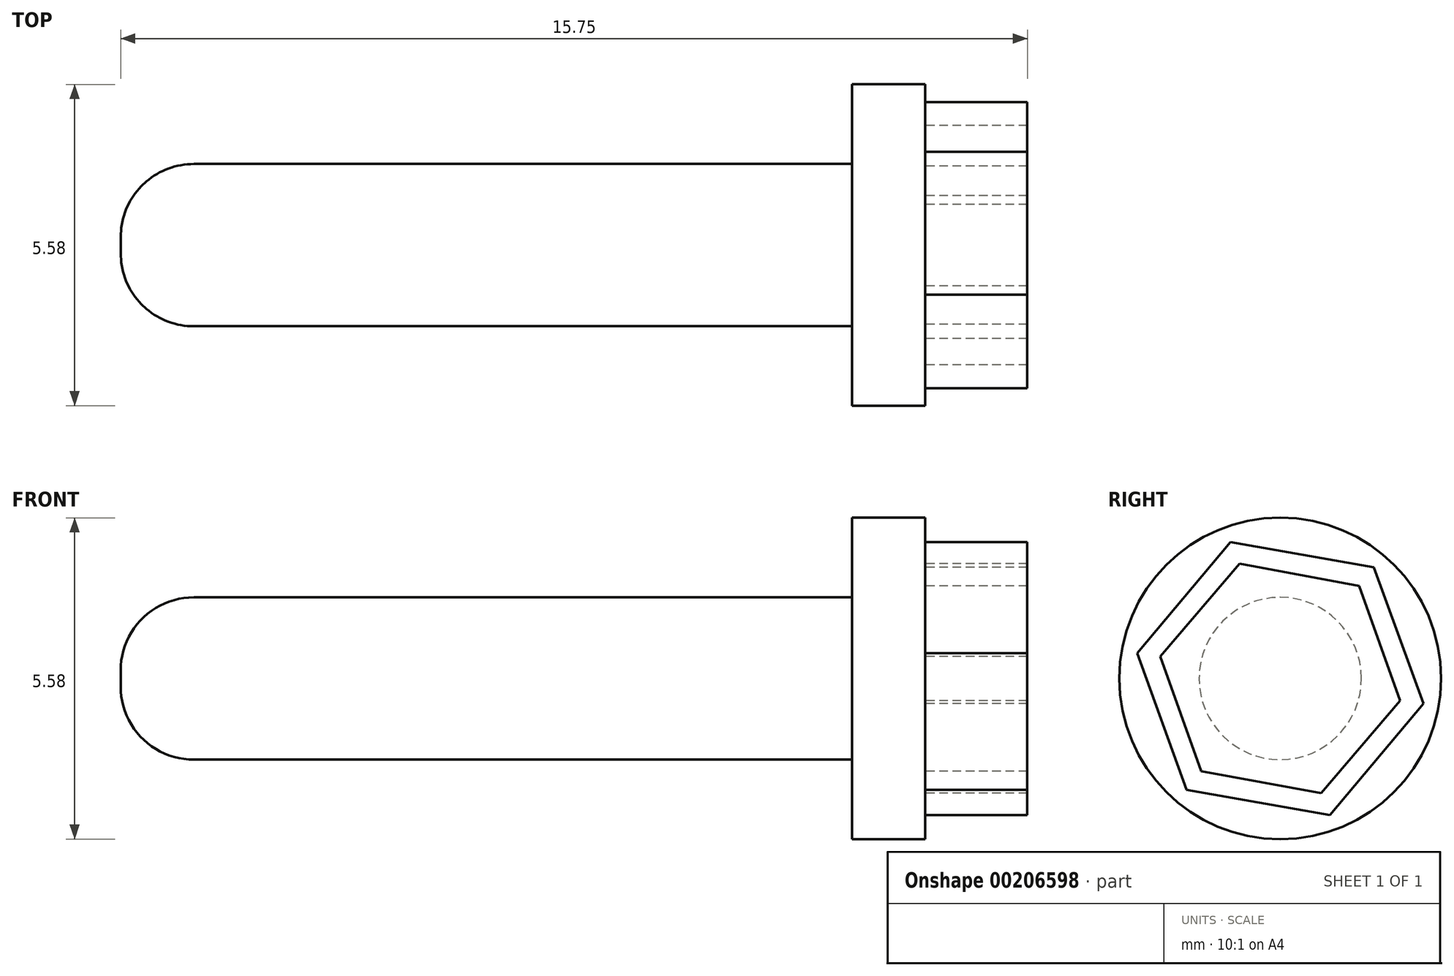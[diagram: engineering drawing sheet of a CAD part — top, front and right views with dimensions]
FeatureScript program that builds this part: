
annotation { "Feature Type Name" : "Feature", "Feature Type Description" : "" }
export const myFeature = defineFeature(function(context is Context, id is Id, definition is map)
    precondition{}
    {
        {
            var Q0;
            Q0=qCreatedBy(makeId("Right.planeOp"),FACE);
            var sketch = newSketch(context, id + "F0", { "sketchPlane" : qUnion([Q0])});
            skCircle(sketch, "E0", {"center": v(0, 0) * mm, "radius": 2.8 * mm});
            skSolve(sketch);
        }
        {
            var Q0;
            Q0=makeQuery(id+"F0.imprint","IMPRINT",FACE,{"disambiguationData":[TD([[makeQuery(id+"F0.imprint","IMPRINT",EDGE,{"derivedFrom":sQuery(id+"F0.wireOp",EDGE,"E0")}),1.0]])]});
            extrude(context, id + "F1", {"entities" : qUnion([Q0]), "depth" : 1.27 * mm});
        }
        {
            var Q0;
            Q0=makeQuery(id+"F1.opExtrude","CAP_FACE",FACE,{"disambiguationData":[OSD([sQuery(id+"F0.wireOp",EDGE,"E0")])],"isStart":false});
            var sketch = newSketch(context, id + "F2", { "sketchPlane" : qUnion([Q0])});
            skCircle(sketch, "E1.cCircle", {"center": v(0, 0) * mm, "radius": 2.19 * mm, "construction": true});
            skLineSegment(sketch, "E1.0", {"start": v(0.86, -2.37) * mm, "end": v(-1.62, -1.93) * mm});
            skLineSegment(sketch, "E1.1", {"start": v(-1.62, -1.93) * mm, "end": v(-2.49, 0.44) * mm});
            skLineSegment(sketch, "E1.2", {"start": v(-2.49, 0.44) * mm, "end": v(-0.86, 2.37) * mm});
            skLineSegment(sketch, "E1.3", {"start": v(-0.86, 2.37) * mm, "end": v(1.62, 1.93) * mm});
            skLineSegment(sketch, "E1.4", {"start": v(1.62, 1.93) * mm, "end": v(2.49, -0.44) * mm});
            skLineSegment(sketch, "E1.5", {"start": v(2.49, -0.44) * mm, "end": v(0.86, -2.37) * mm});
            skPoint(sketch, "E1.0.midPoint", {"position": v(-0.38, -2.15) * mm});
            skCircle(sketch, "E2.cCircle", {"center": v(0, 0) * mm, "radius": 1.83 * mm, "construction": true});
            skLineSegment(sketch, "E2.0", {"start": v(0.7, -2) * mm, "end": v(-1.37, -1.6) * mm});
            skLineSegment(sketch, "E2.1", {"start": v(-1.37, -1.6) * mm, "end": v(-2.08, 0.38) * mm});
            skLineSegment(sketch, "E2.2", {"start": v(-2.08, 0.38) * mm, "end": v(-0.7, 2) * mm});
            skLineSegment(sketch, "E2.3", {"start": v(-0.7, 2) * mm, "end": v(1.37, 1.6) * mm});
            skLineSegment(sketch, "E2.4", {"start": v(1.37, 1.6) * mm, "end": v(2.08, -0.38) * mm});
            skLineSegment(sketch, "E2.5", {"start": v(2.08, -0.38) * mm, "end": v(0.7, -2) * mm});
            skPoint(sketch, "E2.0.midPoint", {"position": v(-0.33, -1.8) * mm});
            skSolve(sketch);
        }
        {
            var Q0;
            Q0=makeQuery(id+"F2.imprint","IMPRINT",FACE,{"disambiguationData":[TD([[makeQuery(id+"F2.imprint","IMPRINT",EDGE,{"derivedFrom":sQuery(id+"F2.wireOp",EDGE,"E1.0")}),-1.0]])]});
            extrude(context, id + "F3", {"entities" : qUnion([Q0]), "operationType" : NewBodyOperationType.ADD, "depth" : 1.78 * mm});
        }
        {
            var Q0;
            Q0=makeQuery(id+"F1.opExtrude","CAP_FACE",FACE,{"disambiguationData":[OSD([sQuery(id+"F0.wireOp",EDGE,"E0")])],"isStart":true});
            var sketch = newSketch(context, id + "F4", { "sketchPlane" : qUnion([Q0])});
            skCircle(sketch, "E3", {"center": v(0, 0) * mm, "radius": 1.4 * mm});
            skSolve(sketch);
        }
        {
            var Q0;
            Q0=makeQuery(id+"F4.imprint","IMPRINT",FACE,{"disambiguationData":[TD([[makeQuery(id+"F4.imprint","IMPRINT",EDGE,{"derivedFrom":sQuery(id+"F4.wireOp",EDGE,"E3")}),1.0]])]});
            extrude(context, id + "F5", {"entities" : qUnion([Q0]), "operationType" : NewBodyOperationType.ADD, "depth" : 12.7 * mm});
        }
        {
            var Q0;
            Q0=makeQuery(id+"F5.opExtrude","CAP_FACE",FACE,{"disambiguationData":[OSD([sQuery(id+"F4.wireOp",EDGE,"E3")])],"isStart":false});
            fillet(context, id + "F6", {"entities" : qUnion([Q0]), "radius" : 1.27 * mm, "tangentPropagation" : true, "allowEdgeOverflow" : false});
        }
    });
